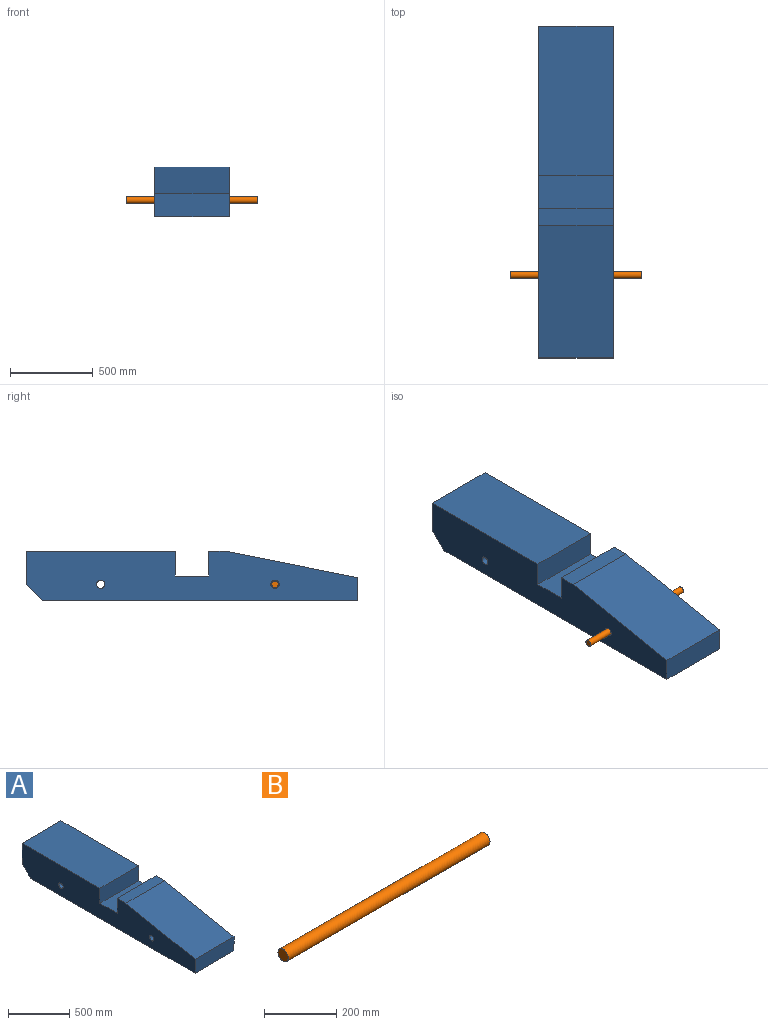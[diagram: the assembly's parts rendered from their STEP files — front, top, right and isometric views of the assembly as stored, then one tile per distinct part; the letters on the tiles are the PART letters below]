
ASSEMBLY  parts=2 mates=1
PART A: 14 faces, bbox 450x2000x300 mm
  f0: plane 450x140mm, normal (0,-1,0), area 63000mm2, adj f1,f10,f11,f12
  f1: plane 1900x450mm, normal (0,0,-1), area 855000mm2, adj f0,f11,f12,f13
  f2: plane 450x200mm, normal (0,1,0), area 90000mm2, adj f3,f11,f12,f13
  f3: plane 900x450mm, normal (0,0,1), area 405000mm2, adj f2,f4,f11,f12
  f4: plane 450x150mm, normal (0,-1,0), area 67500mm2, adj f3,f5,f11,f12
  f5: plane 450x200mm, normal (0,0,1), area 90000mm2, adj f4,f6,f11,f12
  f6: plane 450x150mm, normal (0,1,0), area 67500mm2, adj f5,f7,f11,f12
  f7: plane 450x100mm, normal (0,0,1), area 45000mm2, adj f6,f10,f11,f12
  f8: cylinder r=25mm len=450mm, axis (1,0,0), area 70685.8mm2, adj f11,f12
  f9: cylinder r=25mm len=450mm, axis (1,0,0), area 70685.8mm2, adj f11,f12
  f10: plane 800x450mm, normal (0,-0.2,0.98), area 367129.4mm2, adj f0,f7,f11,f12
  f11: plane 2000x300mm, normal (-1,0,0), area 497073mm2, adj f0,f1,f2,f3,f4,f5,f6,f7
  f12: plane 2000x300mm, normal (1,0,0), area 497073mm2, adj f0,f1,f2,f3,f4,f5,f6,f7
  f13: plane 450x100mm, normal (0,0.71,-0.71), area 63639.6mm2, adj f1,f2,f11,f12
PART B: 3 faces, bbox 790x40x40 mm
  f0: cylinder r=20mm len=790mm, axis (1,0,0), area 99274.3mm2, adj f1,f2
  f1: plane 40x40mm, normal (-1,0,0), area 1256.6mm2, adj f0
  f2: plane 40x40mm, normal (1,0,0), area 1256.6mm2, adj f0
PLACE A at identity fixed
PLACE B t=(170,500,-40)mm
MATE revolute B.f0 <-> A.f8  axis (1,0,0) through (170,500,-40)mm
